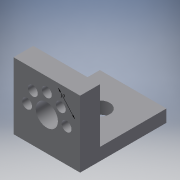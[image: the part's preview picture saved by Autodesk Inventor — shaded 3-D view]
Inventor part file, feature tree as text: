
AUTODESK INVENTOR PART (.ipt)
format: ipt  version: 2016 (Build 200138000, 138)  size: 139,264 bytes
history: native  units: mm
features: sketch x5, reference x5, extrude x3, hole x2
ambient origin geometry x8: Origin, YZ Plane, XZ Plane, XY Plane, X Axis, Y Axis, Z Axis, Center Point
bodies: Body1 (feature_tree)
feature tree (15):
  extrude  "Extrusion2"  Depth=27.0mm
  extrude  "Extrusion4"  Depth=8.0mm TaperAngle=0.0deg
  hole  "Hole1"  [1 undecoded]
  hole  "Hole2"  [1 undecoded]
  extrude  "Extrusion5"  Depth=8.0mm
  sketch  "Sketch1"  dims[d0=27.0mm d1=27.0mm]
  sketch  "Sketch4"  dims[d5=7.0mm d6=8.0mm d7=0.0mm]
  sketch  "Sketch5"  dims[d11=27.0mm d12=5.0mm]
  sketch  "Sketch7"  dims[d13=27.0mm d14=0.0mm d15=27.0mm]
  reference  "Reference2"
  reference  "Reference3"
  reference  "Reference4"
  reference  "Reference5"
  reference  "Reference6"
  sketch  "Sketch9"  dims[d16=27.0mm d17=8.0mm d18=8.0mm d19=6.0mm d20=4.0mm d21=2.0mm d22=90.0deg d23=5.0mm d24=20.594885mm d25=4.0mm d26=6.0mm d27=4.0mm d28=2.0mm d29=90.0deg d30=8.0mm d31=20.594885mm d33=9.0mm d34=52.0mm d35=0.0mm]
note: 2 required parameter values undecoded (feature->parameter linkage not recoverable at this tier; creation-order binding heuristic only, values carry confidence <= 0.55)
